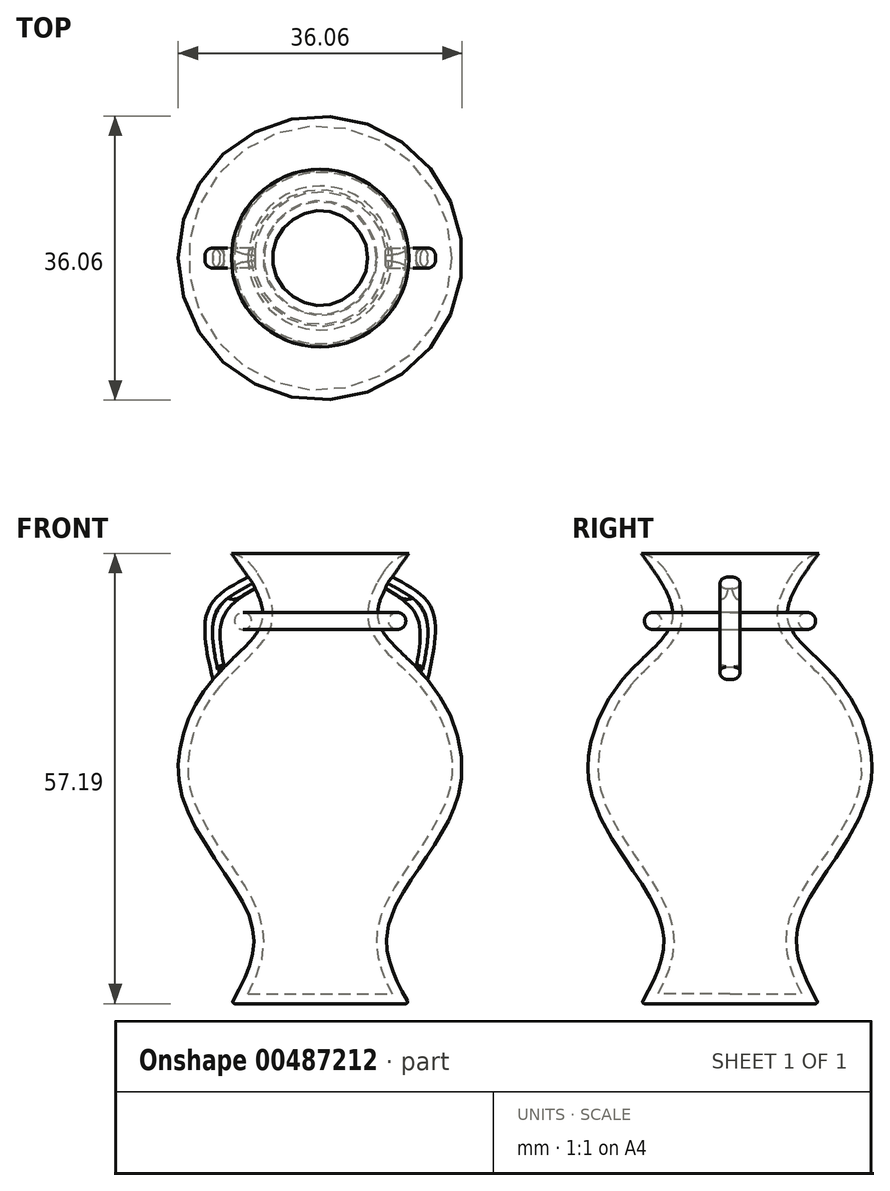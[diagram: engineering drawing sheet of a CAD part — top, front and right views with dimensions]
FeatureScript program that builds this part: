
annotation { "Feature Type Name" : "Feature", "Feature Type Description" : "" }
export const myFeature = defineFeature(function(context is Context, id is Id, definition is map)
    precondition{}
    {
        {
            var Q0;
            Q0=qCreatedBy(makeId("Front.planeOp"),FACE);
            var sketch = newSketch(context, id + "F0", { "sketchPlane" : qUnion([Q0])});
            skLineSegment(sketch, "E0", {"start": v(0, 0) * mm, "end": v(0, 57.19) * mm});
            skLineSegment(sketch, "E1", {"start": v(0, 57.19) * mm, "end": v(11.28, 57.19) * mm});
            skFitSpline(sketch, "E2", {"points": [v(11.28, 57.19) * mm, v(7.35, 48.8) * mm, v(13.64, 41.19) * mm, v(17.58, 26.5) * mm, v(8.66, 9.97) * mm, v(11.28, 0) * mm], "startDerivative": vector(-38, -51.58) * mm, "endDerivative": vector(29.07, -52.28) * mm});
            skLineSegment(sketch, "E3", {"start": v(11.28, 0) * mm, "end": v(0, 0) * mm});
            skFitSpline(sketch, "E4", {"points": [v(9.1, 54.22) * mm, v(14.19, 50.12) * mm, v(13.64, 41.19) * mm], "startDerivative": vector(13.83, -7.12) * mm, "endDerivative": vector(-4.26, -18.64) * mm});
            skFitSpline(sketch, "E5", {"points": [v(8.3, 52.75) * mm, v(12.3, 49.15) * mm, v(12.19, 42.77) * mm], "startDerivative": vector(10.43, -6.38) * mm, "endDerivative": vector(-2.52, -13.52) * mm});
            skLineSegment(sketch, "E6", {"start": v(9.1, 54.22) * mm, "end": v(8.82, 54.37) * mm});
            skLineSegment(sketch, "E7", {"start": v(8.3, 52.75) * mm, "end": v(8.05, 52.9) * mm});
            skLineSegment(sketch, "E8", {"start": v(8.05, 52.9) * mm, "end": v(8.82, 54.37) * mm});
            skLineSegment(sketch, "E9", {"start": v(12.19, 42.77) * mm, "end": v(12.02, 42.54) * mm});
            skLineSegment(sketch, "E10", {"start": v(12.02, 42.54) * mm, "end": v(13.49, 40.9) * mm});
            skLineSegment(sketch, "E11", {"start": v(13.49, 40.9) * mm, "end": v(13.64, 41.19) * mm});
            skCircle(sketch, "E12", {"center": v(9.8, 48.61) * mm, "radius": 1.08 * mm});
            skSolve(sketch);
        }
        {
            var Q0;
            Q0=makeQuery(id+"F0.imprint","IMPRINT",FACE,{"disambiguationData":[TD([[makeQuery(id+"F0.imprint","IMPRINT",EDGE,{"derivedFrom":sQuery(id+"F0.wireOp",EDGE,"E0")}),-1.0]])]});
            var Q1;
            {var subQ1=sQuery(id+"F0.wireOp",EDGE,"E6");Q1=makeQuery(id+"F0.imprint","IMPRINT",FACE,{"disambiguationData":[TD([[makeQuery(id+"F0.imprint","IMPRINT",EDGE,{"derivedFrom":subQ1}),1.0]])]});}
            var Q2;
            {var subQ2=sQuery(id+"F0.wireOp",EDGE,"E9");Q2=makeQuery(id+"F0.imprint","IMPRINT",FACE,{"disambiguationData":[TD([[makeQuery(id+"F0.imprint","IMPRINT",EDGE,{"derivedFrom":subQ2}),1.0]])]});}
            var Q3;
            Q3=makeQuery(id+"F0.imprint","IMPRINT",FACE,{"disambiguationData":[TD([[makeQuery(id+"F0.imprint","IMPRINT",EDGE,{"derivedFrom":sQuery(id+"F0.wireOp",EDGE,"E12")}),1.0]])]});
            var Q4;
            Q4=sQuery(id+"F0.wireOp",EDGE,"E0");
            revolve(context, id + "F1", {"entities" : qUnion([Q0, Q1, Q2, Q3]), "axis" : qUnion([Q4]), "revolveType" : RevolveType.FULL});
        }
        {
            var Q0;
            Q0=makeQuery(id+"F1.opRevolve","SWEPT_FACE",FACE,{"disambiguationData":[OSD([sQuery(id+"F0.wireOp",EDGE,"E1")])]});
            shell(context, id + "F2", {"entities" : qUnion([Q0]), "thickness" : 1.27 * mm});
        }
        {
            var Q0;
            {var subQ0=sQuery(id+"F0.wireOp",EDGE,"E5");Q0=makeQuery(id+"F0.imprint","IMPRINT",FACE,{"disambiguationData":[TD([[makeQuery(id+"F0.imprint","IMPRINT",EDGE,{"derivedFrom":subQ0}),1.0]])]});}
            var Q1;
            {var subQ1=sQuery(id+"F0.wireOp",EDGE,"E6");Q1=makeQuery(id+"F0.imprint","IMPRINT",FACE,{"disambiguationData":[TD([[makeQuery(id+"F0.imprint","IMPRINT",EDGE,{"derivedFrom":subQ1}),1.0]])]});}
            var Q2;
            {var subQ2=sQuery(id+"F0.wireOp",EDGE,"E9");Q2=makeQuery(id+"F0.imprint","IMPRINT",FACE,{"disambiguationData":[TD([[makeQuery(id+"F0.imprint","IMPRINT",EDGE,{"derivedFrom":subQ2}),1.0]])]});}
            extrude(context, id + "F3", {"entities" : qUnion([Q0, Q1, Q2]), "depth" : 1.27 * mm});
        }
        {
            var Q0;
            Q0=makeQuery(id+"F3.opExtrude","SWEPT_BODY",BODY,{"disambiguationData":[OSD([sQuery(id+"F0.wireOp",EDGE,"E2"),sQuery(id+"F0.wireOp",EDGE,"E4"),sQuery(id+"F0.wireOp",EDGE,"E5")])]});
            var Q1;
            Q1=qCreatedBy(makeId("Right.planeOp"),FACE);
            mirror(context, id + "F4", {"entities" : qUnion([Q0]), "mirrorPlane" : qUnion([Q1])});
        }
        {
            var Q0;
            Q0=makeQuery(id+"F3.opExtrude","SWEPT_BODY",BODY,{"disambiguationData":[OSD([sQuery(id+"F0.wireOp",EDGE,"E2"),sQuery(id+"F0.wireOp",EDGE,"E4"),sQuery(id+"F0.wireOp",EDGE,"E5")])]});
            var Q1;
            {var subQ0=sQuery(id+"F0.wireOp",EDGE,"E5");Q1=makeQuery(id+"F0.imprint","IMPRINT",FACE,{"disambiguationData":[TD([[makeQuery(id+"F0.imprint","IMPRINT",EDGE,{"derivedFrom":subQ0}),1.0]])]});}
            mirror(context, id + "F5", {"operationType" : NewBodyOperationType.ADD, "entities" : qUnion([Q0]), "mirrorPlane" : qUnion([Q1])});
        }
        {
            var Q0;
            Q0=makeQuery(id+"F4.opPattern","COPY",BODY,{"derivedFrom":makeQuery(id+"F3.opExtrude","SWEPT_BODY",BODY,{"disambiguationData":[OSD([sQuery(id+"F0.wireOp",EDGE,"E2"),sQuery(id+"F0.wireOp",EDGE,"E4"),sQuery(id+"F0.wireOp",EDGE,"E5")])]}),"instanceName":"1"});
            var Q1;
            Q1=qCreatedBy(makeId("Front.planeOp"),FACE);
            mirror(context, id + "F6", {"operationType" : NewBodyOperationType.ADD, "entities" : qUnion([Q0]), "mirrorPlane" : qUnion([Q1])});
        }
        {
            var Q0;
            Q0=makeQuery(id+"F6.opPattern","COPY",EDGE,{"derivedFrom":makeQuery(id+"F4.opPattern","COPY",EDGE,{"derivedFrom":makeQuery(id+"F3.opExtrude","CAP_EDGE",EDGE,{"disambiguationData":[OSD([sQuery(id+"F0.wireOp",EDGE,"E4")])],"isStart":false}),"instanceName":"1"}),"instanceName":"1"});
            var Q1;
            Q1=makeQuery(id+"F4.opPattern","COPY",EDGE,{"derivedFrom":makeQuery(id+"F3.opExtrude","CAP_EDGE",EDGE,{"disambiguationData":[OSD([sQuery(id+"F0.wireOp",EDGE,"E4")])],"isStart":false}),"instanceName":"1"});
            var Q2;
            Q2=makeQuery(id+"F6.opPattern","COPY",EDGE,{"derivedFrom":makeQuery(id+"F4.opPattern","COPY",EDGE,{"derivedFrom":makeQuery(id+"F3.opExtrude","CAP_EDGE",EDGE,{"disambiguationData":[OSD([sQuery(id+"F0.wireOp",EDGE,"E5")])],"isStart":false}),"instanceName":"1"}),"instanceName":"1"});
            var Q3;
            Q3=makeQuery(id+"F4.opPattern","COPY",EDGE,{"derivedFrom":makeQuery(id+"F3.opExtrude","CAP_EDGE",EDGE,{"disambiguationData":[OSD([sQuery(id+"F0.wireOp",EDGE,"E5")])],"isStart":false}),"instanceName":"1"});
            var Q4;
            Q4=makeQuery(id+"F3.opExtrude","CAP_EDGE",EDGE,{"disambiguationData":[OSD([sQuery(id+"F0.wireOp",EDGE,"E5")])],"isStart":false});
            var Q5;
            Q5=makeQuery(id+"F5.opPattern","COPY",EDGE,{"derivedFrom":makeQuery(id+"F3.opExtrude","CAP_EDGE",EDGE,{"disambiguationData":[OSD([sQuery(id+"F0.wireOp",EDGE,"E5")])],"isStart":false}),"instanceName":"1"});
            var Q6;
            Q6=makeQuery(id+"F3.opExtrude","CAP_EDGE",EDGE,{"disambiguationData":[OSD([sQuery(id+"F0.wireOp",EDGE,"E4")])],"isStart":false});
            var Q7;
            Q7=makeQuery(id+"F5.opPattern","COPY",EDGE,{"derivedFrom":makeQuery(id+"F3.opExtrude","CAP_EDGE",EDGE,{"disambiguationData":[OSD([sQuery(id+"F0.wireOp",EDGE,"E4")])],"isStart":false}),"instanceName":"1"});
            fillet(context, id + "F7", {"entities" : qUnion([Q0, Q1, Q2, Q3, Q4, Q5, Q6, Q7]), "radius" : 1.02 * mm, "tangentPropagation" : true, "allowEdgeOverflow" : false});
        }
        {
            var Q0;
            Q0=makeQuery(id+"F3.opExtrude","CAP_EDGE",EDGE,{"disambiguationData":[OSD([sQuery(id+"F0.wireOp",EDGE,"E7")])],"isStart":false});
            fillet(context, id + "F8", {"entities" : qUnion([Q0]), "radius" : 0.76 * mm, "tangentPropagation" : true, "allowEdgeOverflow" : false});
        }
        {
            var Q0;
            Q0=makeQuery(id+"F3.opExtrude","CAP_EDGE",EDGE,{"disambiguationData":[OSD([sQuery(id+"F0.wireOp",EDGE,"E9")])],"isStart":false});
            fillet(context, id + "F9", {"entities" : qUnion([Q0]), "radius" : 0.76 * mm, "tangentPropagation" : true, "allowEdgeOverflow" : false});
        }
        {
            var Q0;
            Q0=makeQuery(id+"F5.opPattern","COPY",EDGE,{"derivedFrom":makeQuery(id+"F3.opExtrude","CAP_EDGE",EDGE,{"disambiguationData":[OSD([sQuery(id+"F0.wireOp",EDGE,"E7")])],"isStart":false}),"instanceName":"1"});
            var Q1;
            Q1=makeQuery(id+"F6.opPattern","COPY",EDGE,{"derivedFrom":makeQuery(id+"F4.opPattern","COPY",EDGE,{"derivedFrom":makeQuery(id+"F3.opExtrude","CAP_EDGE",EDGE,{"disambiguationData":[OSD([sQuery(id+"F0.wireOp",EDGE,"E7")])],"isStart":false}),"instanceName":"1"}),"instanceName":"1"});
            var Q2;
            Q2=makeQuery(id+"F5.opPattern","COPY",EDGE,{"derivedFrom":makeQuery(id+"F3.opExtrude","CAP_EDGE",EDGE,{"disambiguationData":[OSD([sQuery(id+"F0.wireOp",EDGE,"E9")])],"isStart":false}),"instanceName":"1"});
            fillet(context, id + "F10", {"entities" : qUnion([Q0, Q1, Q2]), "radius" : 0.76 * mm, "tangentPropagation" : true, "allowEdgeOverflow" : false});
        }
        {
            var Q0;
            Q0=makeQuery(id+"F6.opPattern","COPY",EDGE,{"derivedFrom":makeQuery(id+"F4.opPattern","COPY",EDGE,{"derivedFrom":makeQuery(id+"F3.opExtrude","CAP_EDGE",EDGE,{"disambiguationData":[OSD([sQuery(id+"F0.wireOp",EDGE,"E9")])],"isStart":false}),"instanceName":"1"}),"instanceName":"1"});
            var Q1;
            Q1=makeQuery(id+"F4.opPattern","COPY",EDGE,{"derivedFrom":makeQuery(id+"F3.opExtrude","CAP_EDGE",EDGE,{"disambiguationData":[OSD([sQuery(id+"F0.wireOp",EDGE,"E7")])],"isStart":false}),"instanceName":"1"});
            var Q2;
            Q2=makeQuery(id+"F4.opPattern","COPY",EDGE,{"derivedFrom":makeQuery(id+"F3.opExtrude","CAP_EDGE",EDGE,{"disambiguationData":[OSD([sQuery(id+"F0.wireOp",EDGE,"E9")])],"isStart":false}),"instanceName":"1"});
            fillet(context, id + "F11", {"entities" : qUnion([Q0, Q1, Q2]), "radius" : 0.76 * mm, "tangentPropagation" : true, "allowEdgeOverflow" : false});
        }
        {
            var Q0;
            Q0=makeQuery(id+"F2.opShell","OFFSET_EDGE",EDGE,{"disambiguationData":[OSD([sQuery(id+"F0.wireOp",EDGE,"E1"),sQuery(id+"F0.wireOp",EDGE,"E2")])]});
            fillet(context, id + "F12", {"entities" : qUnion([Q0]), "radius" : 5.08 * mm, "tangentPropagation" : true, "allowEdgeOverflow" : false});
        }
        {
            var Q0;
            Q0=makeQuery(id+"F1.opRevolve","SWEPT_EDGE",EDGE,{"disambiguationData":[OSD([sQuery(id+"F0.wireOp",EDGE,"E2"),sQuery(id+"F0.wireOp",EDGE,"E3")])]});
            fillet(context, id + "F13", {"entities" : qUnion([Q0]), "radius" : 0.25 * mm, "tangentPropagation" : true, "allowEdgeOverflow" : false});
        }
    });
